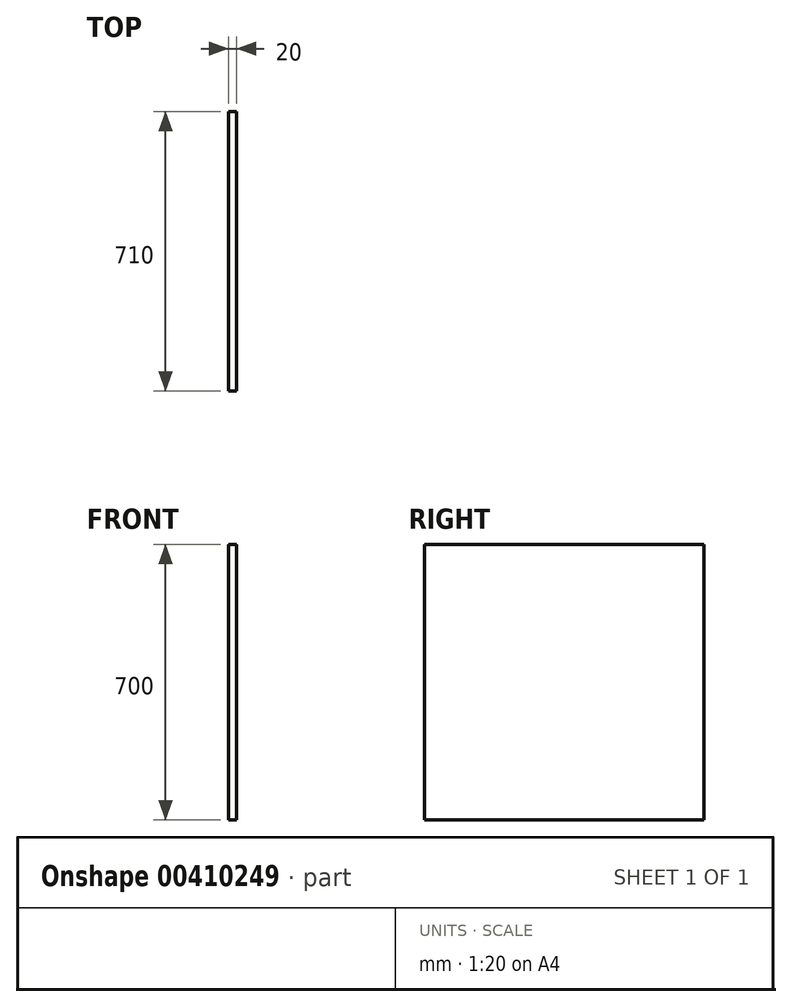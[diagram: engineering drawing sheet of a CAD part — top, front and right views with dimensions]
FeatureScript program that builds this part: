
annotation { "Feature Type Name" : "Feature", "Feature Type Description" : "" }
export const myFeature = defineFeature(function(context is Context, id is Id, definition is map)
    precondition{}
    {
        {
            var Q0;
            Q0=qCreatedBy(makeId("Right.planeOp"),FACE);
            var sketch = newSketch(context, id + "F0", { "sketchPlane" : qUnion([Q0])});
            skLineSegment(sketch, "E0.bottom", {"start": v(355, 350) * mm, "end": v(-355, 350) * mm});
            skLineSegment(sketch, "E0.top", {"start": v(355, -350) * mm, "end": v(-355, -350) * mm});
            skLineSegment(sketch, "E0.left", {"start": v(355, 350) * mm, "end": v(355, -350) * mm});
            skLineSegment(sketch, "E0.right", {"start": v(-355, 350) * mm, "end": v(-355, -350) * mm});
            skPoint(sketch, "E0.middle", {"position": v(0, 0) * mm});
            skSolve(sketch);
        }
        {
            var Q0;
            Q0 = qSketchRegion(id + "F0", true);
            extrude(context, id + "F1", {"entities" : qUnion([Q0]), "flatOperationType" : FlatOperationType.REMOVE, "endBound" : BoundingType.SYMMETRIC, "offsetDistance" : 25 * mm, "depth" : 20 * mm, "domain" : OperationDomain.MODEL});
        }
    });
